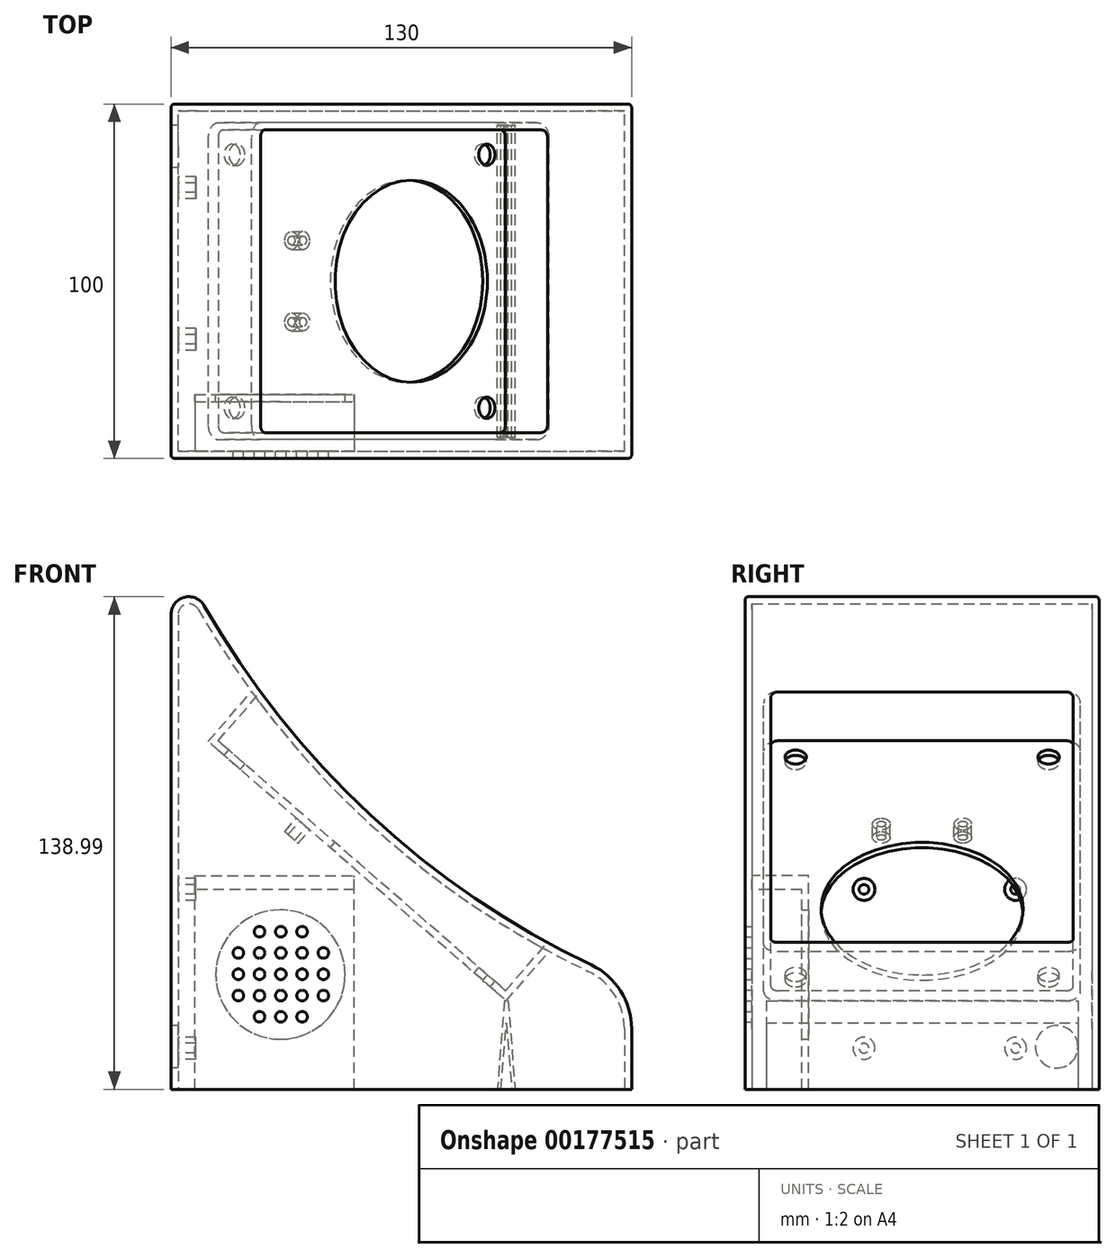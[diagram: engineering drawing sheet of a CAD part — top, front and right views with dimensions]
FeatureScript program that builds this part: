
annotation { "Feature Type Name" : "Feature", "Feature Type Description" : "" }
export const myFeature = defineFeature(function(context is Context, id is Id, definition is map)
    precondition{}
    {
        {
            var Q0;
            Q0=qCreatedBy(makeId("Front.planeOp"),FACE);
            var sketch = newSketch(context, id + "F0", { "sketchPlane" : qUnion([Q0])});
            skLineSegment(sketch, "E0", {"start": v(-84.02, -67.29) * mm, "end": v(45.98, -67.29) * mm});
            skPoint(sketch, "E1.visualSharp", {"position": v(-84.02, 87.14) * mm});
            skPoint(sketch, "E2.visualSharp", {"position": v(45.98, -37.29) * mm});
            skArc(sketch, "E3", {"start": v(-74.68, 69.19) * mm, "mid": v(-23.15, 5.98) * mm, "end": v(45.98, -37.29) * mm});
            skLineSegment(sketch, "E4", {"start": v(-84.02, 66.7) * mm, "end": v(-84.02, -67.29) * mm});
            skLineSegment(sketch, "E5", {"start": v(45.98, -37.29) * mm, "end": v(45.98, -67.29) * mm});
            skArc(sketch, "E6.filletArc", {"start": v(-74.68, 69.19) * mm, "mid": v(-80.3, 71.53) * mm, "end": v(-84.02, 66.7) * mm});
            skSolve(sketch);
        }
        {
            var Q0;
            Q0=makeQuery(id+"F0.imprint","IMPRINT",FACE,{"disambiguationData":[TD([[makeQuery(id+"F0.imprint","IMPRINT",EDGE,{"derivedFrom":sQuery(id+"F0.wireOp",EDGE,"E0")}),1.0]])]});
            extrude(context, id + "F1", {"entities" : qUnion([Q0]), "depth" : 100 * mm, "symmetric" : true});
        }
        {
            var Q0;
            Q0=makeQuery(id+"F1.opExtrude","SWEPT_EDGE",EDGE,{"disambiguationData":[OSD([sQuery(id+"F0.wireOp",EDGE,"E3"),sQuery(id+"F0.wireOp",EDGE,"E5")])]});
            cPlane(context, id + "F2", {"entities" : qUnion([Q0]), "cplaneType" : CPlaneType.LINE_ANGLE, "offset" : 25 * mm, "angle" : 41 * degree, "width" : 150 * mm, "height" : 150 * mm});
        }
        {
            var Q0;
            Q0=qCreatedBy(id+"F2.planeOp",FACE);
            var sketch = newSketch(context, id + "F3", { "sketchPlane" : qUnion([Q0])});
            skLineSegment(sketch, "E7.bottom", {"start": v(31.75, 42.7) * mm, "end": v(-71.75, 42.7) * mm});
            skLineSegment(sketch, "E7.top", {"start": v(31.75, -42.7) * mm, "end": v(-71.75, -42.7) * mm});
            skLineSegment(sketch, "E7.left", {"start": v(33.75, 40.7) * mm, "end": v(33.75, -40.7) * mm});
            skLineSegment(sketch, "E7.right", {"start": v(-73.75, 40.7) * mm, "end": v(-73.75, -40.7) * mm});
            skPoint(sketch, "E7.middle", {"position": v(-20, 0) * mm});
            skPoint(sketch, "E8.visualSharp", {"position": v(-73.75, -42.7) * mm});
            skArc(sketch, "E8.filletArc", {"start": v(-73.75, -40.7) * mm, "mid": v(-73.16, -42.11) * mm, "end": v(-71.75, -42.7) * mm});
            skPoint(sketch, "E9.visualSharp", {"position": v(-73.75, 42.7) * mm});
            skArc(sketch, "E9.filletArc", {"start": v(-71.75, 42.7) * mm, "mid": v(-73.16, 42.11) * mm, "end": v(-73.75, 40.7) * mm});
            skPoint(sketch, "E10.visualSharp", {"position": v(33.75, 42.7) * mm});
            skArc(sketch, "E10.filletArc", {"start": v(33.75, 40.7) * mm, "mid": v(33.16, 42.11) * mm, "end": v(31.75, 42.7) * mm});
            skPoint(sketch, "E11.visualSharp", {"position": v(33.75, -42.7) * mm});
            skArc(sketch, "E11.filletArc", {"start": v(31.75, -42.7) * mm, "mid": v(33.16, -42.11) * mm, "end": v(33.75, -40.7) * mm});
            skCircle(sketch, "E12", {"center": v(-1.55, 0) * mm, "radius": 28.5 * mm});
            skCircle(sketch, "E13", {"center": v(-66.75, -35.7) * mm, "radius": 3 * mm});
            skCircle(sketch, "E14", {"center": v(-66.75, 35.7) * mm, "radius": 3 * mm});
            skCircle(sketch, "E15", {"center": v(26.75, 35.7) * mm, "radius": 3 * mm});
            skCircle(sketch, "E16", {"center": v(26.75, -35.7) * mm, "radius": 3 * mm});
            skSolve(sketch);
        }
        {
            var Q0;
            Q0=makeQuery(id+"F3.imprint","IMPRINT",FACE,{"disambiguationData":[TD([[makeQuery(id+"F3.imprint","IMPRINT",EDGE,{"derivedFrom":sQuery(id+"F3.wireOp",EDGE,"E7.bottom")}),1.0]])]});
            var Q1;
            Q1=makeQuery(id+"F3.imprint","IMPRINT",FACE,{"disambiguationData":[TD([[makeQuery(id+"F3.imprint","IMPRINT",EDGE,{"derivedFrom":sQuery(id+"F3.wireOp",EDGE,"E12")}),1.0]])]});
            var Q2;
            Q2=makeQuery(id+"F3.imprint","IMPRINT",FACE,{"disambiguationData":[TD([[makeQuery(id+"F3.imprint","IMPRINT",EDGE,{"derivedFrom":sQuery(id+"F3.wireOp",EDGE,"E14")}),1.0]])]});
            var Q3;
            Q3=makeQuery(id+"F3.imprint","IMPRINT",FACE,{"disambiguationData":[TD([[makeQuery(id+"F3.imprint","IMPRINT",EDGE,{"derivedFrom":sQuery(id+"F3.wireOp",EDGE,"E15")}),1.0]])]});
            var Q4;
            Q4=makeQuery(id+"F3.imprint","IMPRINT",FACE,{"disambiguationData":[TD([[makeQuery(id+"F3.imprint","IMPRINT",EDGE,{"derivedFrom":sQuery(id+"F3.wireOp",EDGE,"E16")}),1.0]])]});
            var Q5;
            Q5=makeQuery(id+"F3.imprint","IMPRINT",FACE,{"disambiguationData":[TD([[makeQuery(id+"F3.imprint","IMPRINT",EDGE,{"derivedFrom":sQuery(id+"F3.wireOp",EDGE,"E13")}),1.0]])]});
            extrude(context, id + "F4", {"entities" : qUnion([Q0, Q1, Q2, Q3, Q4, Q5]), "operationType" : NewBodyOperationType.REMOVE, "oppositeDirection" : true, "depth" : 25 * mm});
        }
        {
            var Q0;
            Q0=makeQuery(id+"F1.opExtrude","SWEPT_EDGE",EDGE,{"disambiguationData":[OSD([sQuery(id+"F0.wireOp",EDGE,"E3"),sQuery(id+"F0.wireOp",EDGE,"E5")])]});
            fillet(context, id + "F5", {"entities" : qUnion([Q0]), "radius" : 20 * mm, "tangentPropagation" : true, "allowEdgeOverflow" : false});
        }
        {
            var Q0;
            Q0=makeQuery(id+"F1.opExtrude","SWEPT_FACE",FACE,{"disambiguationData":[OSD([sQuery(id+"F0.wireOp",EDGE,"E0")])]});
            shell(context, id + "F6", {"entities" : qUnion([Q0]), "thickness" : 2 * mm});
        }
        {
            var Q0;
            Q0=makeQuery(id+"F3.imprint","IMPRINT",FACE,{"disambiguationData":[TD([[makeQuery(id+"F3.imprint","IMPRINT",EDGE,{"derivedFrom":sQuery(id+"F3.wireOp",EDGE,"E12")}),1.0]])]});
            var Q1;
            Q1=makeQuery(id+"F3.imprint","IMPRINT",FACE,{"disambiguationData":[TD([[makeQuery(id+"F3.imprint","IMPRINT",EDGE,{"derivedFrom":sQuery(id+"F3.wireOp",EDGE,"E14")}),1.0]])]});
            var Q2;
            Q2=makeQuery(id+"F3.imprint","IMPRINT",FACE,{"disambiguationData":[TD([[makeQuery(id+"F3.imprint","IMPRINT",EDGE,{"derivedFrom":sQuery(id+"F3.wireOp",EDGE,"E13")}),1.0]])]});
            var Q3;
            Q3=makeQuery(id+"F3.imprint","IMPRINT",FACE,{"disambiguationData":[TD([[makeQuery(id+"F3.imprint","IMPRINT",EDGE,{"derivedFrom":sQuery(id+"F3.wireOp",EDGE,"E15")}),1.0]])]});
            var Q4;
            Q4=makeQuery(id+"F3.imprint","IMPRINT",FACE,{"disambiguationData":[TD([[makeQuery(id+"F3.imprint","IMPRINT",EDGE,{"derivedFrom":sQuery(id+"F3.wireOp",EDGE,"E16")}),1.0]])]});
            extrude(context, id + "F7", {"entities" : qUnion([Q0, Q1, Q2, Q3, Q4]), "operationType" : NewBodyOperationType.REMOVE, "oppositeDirection" : true, "depth" : 40 * mm});
        }
        {
            var Q0;
            Q0=makeQuery(id+"F1.opExtrude","SWEPT_FACE",FACE,{"disambiguationData":[OSD([sQuery(id+"F0.wireOp",EDGE,"E4")])]});
            var sketch = newSketch(context, id + "F8", { "sketchPlane" : qUnion([Q0])});
            skCircle(sketch, "E17", {"center": v(0, 42.55) * mm, "radius": 25 * mm, "construction": true});
            skLineSegment(sketch, "E18", {"start": v(0, 0) * mm, "end": v(0, -62.03) * mm, "construction": true});
            skLineSegment(sketch, "E19", {"start": v(-40.29, 42.55) * mm, "end": v(40.58, 42.55) * mm, "construction": true});
            skLineSegment(sketch, "E20", {"start": v(-40.29, 48.55) * mm, "end": v(40.58, 48.55) * mm, "construction": true});
            skLineSegment(sketch, "E21", {"start": v(-40.29, 36.55) * mm, "end": v(40.58, 36.55) * mm, "construction": true});
            skLineSegment(sketch, "E22", {"start": v(-40.29, 30.55) * mm, "end": v(40.58, 30.55) * mm, "construction": true});
            skLineSegment(sketch, "E23", {"start": v(-40.29, 54.55) * mm, "end": v(40.58, 54.55) * mm, "construction": true});
            skLineSegment(sketch, "E24", {"start": v(-6, 0) * mm, "end": v(-6, -62.03) * mm, "construction": true});
            skLineSegment(sketch, "E25", {"start": v(6, 0) * mm, "end": v(6, -62.03) * mm, "construction": true});
            skLineSegment(sketch, "E26", {"start": v(12, 0) * mm, "end": v(12, -62.03) * mm, "construction": true});
            skLineSegment(sketch, "E27", {"start": v(-12, 0) * mm, "end": v(-12, -62.03) * mm, "construction": true});
            skCircle(sketch, "E28", {"center": v(0, 42.55) * mm, "radius": 1.5 * mm});
            skCircle(sketch, "E29", {"center": v(6, 42.55) * mm, "radius": 1.5 * mm});
            skCircle(sketch, "E30", {"center": v(12, 42.55) * mm, "radius": 1.5 * mm});
            skCircle(sketch, "E31", {"center": v(-6, 42.55) * mm, "radius": 1.5 * mm});
            skCircle(sketch, "E32", {"center": v(-12, 42.55) * mm, "radius": 1.5 * mm});
            skCircle(sketch, "E33", {"center": v(0, 48.55) * mm, "radius": 1.5 * mm});
            skCircle(sketch, "E34", {"center": v(6, 48.55) * mm, "radius": 1.5 * mm});
            skCircle(sketch, "E35", {"center": v(-6, 48.55) * mm, "radius": 1.5 * mm});
            skCircle(sketch, "E36", {"center": v(-6, 54.55) * mm, "radius": 1.5 * mm});
            skCircle(sketch, "E37", {"center": v(0, 54.55) * mm, "radius": 1.5 * mm});
            skCircle(sketch, "E38", {"center": v(6, 54.55) * mm, "radius": 1.5 * mm});
            skCircle(sketch, "E39", {"center": v(12, 48.55) * mm, "radius": 1.5 * mm});
            skCircle(sketch, "E40", {"center": v(12, 36.55) * mm, "radius": 1.5 * mm});
            skCircle(sketch, "E41", {"center": v(6, 36.55) * mm, "radius": 1.5 * mm});
            skCircle(sketch, "E42", {"center": v(0, 36.55) * mm, "radius": 1.5 * mm});
            skCircle(sketch, "E43", {"center": v(-6, 36.55) * mm, "radius": 1.5 * mm});
            skCircle(sketch, "E44", {"center": v(-12, 36.55) * mm, "radius": 1.5 * mm});
            skCircle(sketch, "E45", {"center": v(-6, 30.55) * mm, "radius": 1.5 * mm});
            skCircle(sketch, "E46", {"center": v(0, 30.55) * mm, "radius": 1.5 * mm});
            skCircle(sketch, "E47", {"center": v(6, 30.55) * mm, "radius": 1.5 * mm});
            skCircle(sketch, "E48", {"center": v(-12, 48.55) * mm, "radius": 1.5 * mm});
            skCircle(sketch, "E49", {"center": v(-38, -55.29) * mm, "radius": 6 * mm});
            skLineSegment(sketch, "E50.bottom", {"start": v(42.5, -55.96) * mm, "end": v(-42.5, -55.96) * mm, "construction": true});
            skLineSegment(sketch, "E50.top", {"start": v(42.5, 0.04) * mm, "end": v(-42.5, 0.04) * mm, "construction": true});
            skLineSegment(sketch, "E50.left", {"start": v(42.5, -55.96) * mm, "end": v(42.5, 0.04) * mm, "construction": true});
            skLineSegment(sketch, "E50.right", {"start": v(-42.5, -55.96) * mm, "end": v(-42.5, 0.04) * mm, "construction": true});
            skPoint(sketch, "E50.middle", {"position": v(0, -27.96) * mm});
            skSolve(sketch);
        }
        {
            var Q0;
            Q0=makeQuery(id+"F8.imprint","IMPRINT",FACE,{"disambiguationData":[TD([[makeQuery(id+"F8.imprint","IMPRINT",EDGE,{"derivedFrom":sQuery(id+"F8.wireOp",EDGE,"E49")}),1.0]])]});
            extrude(context, id + "F9", {"entities" : qUnion([Q0]), "operationType" : NewBodyOperationType.REMOVE, "oppositeDirection" : true, "depth" : 25 * mm});
        }
        {
            var Q0;
            Q0=makeQuery(id+"F1.opExtrude","CAP_EDGE",EDGE,{"disambiguationData":[OSD([sQuery(id+"F0.wireOp",EDGE,"E3")])],"isStart":false});
            var Q1;
            Q1=makeQuery(id+"F1.opExtrude","CAP_EDGE",EDGE,{"disambiguationData":[OSD([sQuery(id+"F0.wireOp",EDGE,"E3")])],"isStart":true});
            fillet(context, id + "F10", {"entities" : qUnion([Q0, Q1]), "radius" : 1 * mm, "tangentPropagation" : true, "allowEdgeOverflow" : false});
        }
        {
            var Q0;
            Q0=makeQuery(id+"F6.opShell","OFFSET_FACE",FACE,{"disambiguationData":[OSD([sQuery(id+"F3.wireOp",EDGE,"E7.bottom"),sQuery(id+"F3.wireOp",EDGE,"E7.top"),sQuery(id+"F3.wireOp",EDGE,"E7.left"),sQuery(id+"F3.wireOp",EDGE,"E7.right"),sQuery(id+"F3.wireOp",EDGE,"E8.filletArc"),sQuery(id+"F3.wireOp",EDGE,"E9.filletArc"),sQuery(id+"F3.wireOp",EDGE,"E10.filletArc"),sQuery(id+"F3.wireOp",EDGE,"E11.filletArc")])]});
            cPlane(context, id + "F11", {"entities" : qUnion([Q0]), "cplaneType" : CPlaneType.OFFSET, "offset" : 0 * mm, "width" : 150 * mm, "height" : 150 * mm});
        }
        {
            var Q0;
            Q0=qCreatedBy(id+"F11.planeOp",FACE);
            var sketch = newSketch(context, id + "F12", { "sketchPlane" : qUnion([Q0])});
            skLineSegment(sketch, "E51.bottom", {"start": v(-38, 14) * mm, "end": v(-62, 14) * mm, "construction": true});
            skLineSegment(sketch, "E51.top", {"start": v(-38, -14) * mm, "end": v(-62, -14) * mm, "construction": true});
            skLineSegment(sketch, "E51.left", {"start": v(-38, 14) * mm, "end": v(-38, -14) * mm, "construction": true});
            skLineSegment(sketch, "E51.right", {"start": v(-62, 14) * mm, "end": v(-62, -14) * mm, "construction": true});
            skPoint(sketch, "E51.middle", {"position": v(-50, 0) * mm});
            skCircle(sketch, "E52", {"center": v(-40.24, 11.5) * mm, "radius": 1.25 * mm});
            skCircle(sketch, "E53", {"center": v(-40.24, -11.5) * mm, "radius": 1.25 * mm});
            skCircle(sketch, "E54", {"center": v(-40.24, 11.5) * mm, "radius": 2.5 * mm});
            skCircle(sketch, "E55", {"center": v(-40.24, -11.5) * mm, "radius": 2.5 * mm});
            skSolve(sketch);
        }
        {
            var Q0;
            {var subQ0=sQuery(id+"F0.wireOp",EDGE,"E6.filletArc");var subQ1=sQuery(id+"F0.wireOp",EDGE,"E5");var subQ2=sQuery(id+"F0.wireOp",EDGE,"E4");var subQ3=sQuery(id+"F0.wireOp",EDGE,"E3");var subQ4=sQuery(id+"F0.wireOp",EDGE,"E0");Q0=makeQuery(id+"F6.opShell","OFFSET_FACE",FACE,{"disambiguationData":[OSD([subQ4,subQ3,subQ2,subQ1,subQ0]),TDD([makeQuery(id+"F1.opExtrude","CAP_FACE",FACE,{"disambiguationData":[OSD([subQ4,subQ3,subQ2,subQ1,subQ0])],"isStart":false})])]});}
            var sketch = newSketch(context, id + "F13", { "sketchPlane" : qUnion([Q0])});
            skPoint(sketch, "E56.centerSnap0", {"position": v(36.97, -30.82) * mm});
            skCircle(sketch, "E57", {"center": v(53.03, -34.83) * mm, "radius": 1.5 * mm});
            skCircle(sketch, "E58", {"center": v(59.03, -34.83) * mm, "radius": 1.5 * mm});
            skCircle(sketch, "E59", {"center": v(65.03, -34.83) * mm, "radius": 1.5 * mm});
            skCircle(sketch, "E60", {"center": v(47.03, -34.83) * mm, "radius": 1.5 * mm});
            skCircle(sketch, "E61", {"center": v(41.03, -34.83) * mm, "radius": 1.5 * mm});
            skCircle(sketch, "E62", {"center": v(53.03, -28.83) * mm, "radius": 1.5 * mm});
            skCircle(sketch, "E63", {"center": v(59.03, -28.83) * mm, "radius": 1.5 * mm});
            skCircle(sketch, "E64", {"center": v(47.03, -28.83) * mm, "radius": 1.5 * mm});
            skCircle(sketch, "E65", {"center": v(47.03, -22.83) * mm, "radius": 1.5 * mm});
            skCircle(sketch, "E66", {"center": v(53.03, -22.83) * mm, "radius": 1.5 * mm});
            skCircle(sketch, "E67", {"center": v(59.03, -22.83) * mm, "radius": 1.5 * mm});
            skCircle(sketch, "E68", {"center": v(65.03, -28.83) * mm, "radius": 1.5 * mm});
            skCircle(sketch, "E69", {"center": v(65.03, -40.83) * mm, "radius": 1.5 * mm});
            skCircle(sketch, "E70", {"center": v(59.03, -40.83) * mm, "radius": 1.5 * mm});
            skCircle(sketch, "E71", {"center": v(53.03, -40.83) * mm, "radius": 1.5 * mm});
            skCircle(sketch, "E72", {"center": v(47.03, -40.83) * mm, "radius": 1.5 * mm});
            skCircle(sketch, "E73", {"center": v(41.03, -40.83) * mm, "radius": 1.5 * mm});
            skCircle(sketch, "E74", {"center": v(47.03, -46.83) * mm, "radius": 1.5 * mm});
            skCircle(sketch, "E75", {"center": v(53.03, -46.83) * mm, "radius": 1.5 * mm});
            skCircle(sketch, "E76", {"center": v(59.03, -46.83) * mm, "radius": 1.5 * mm});
            skCircle(sketch, "E77", {"center": v(41.03, -28.83) * mm, "radius": 1.5 * mm});
            skLineSegment(sketch, "E78", {"start": v(65.03, -40.83) * mm, "end": v(41.03, -40.83) * mm});
            skLineSegment(sketch, "E79", {"start": v(59.03, -46.83) * mm, "end": v(47.03, -46.83) * mm});
            skLineSegment(sketch, "E80", {"start": v(65.03, -28.83) * mm, "end": v(41.03, -28.83) * mm});
            skLineSegment(sketch, "E81", {"start": v(59.03, -22.83) * mm, "end": v(47.03, -22.83) * mm});
            skSolve(sketch);
        }
        {
            var Q0;
            {var subQ0=sQuery(id+"F13.wireOp",EDGE,"E80");var subQ1=sQuery(id+"F13.wireOp",EDGE,"E64");var subQ2=makeQuery(id+"F13.imprint","INTERSECT",VERTEX,{"disambiguationData":[OD(0.0)],"derivedFrom":[subQ1,subQ0]});Q0=makeQuery(id+"F13.imprint","IMPRINT",FACE,{"disambiguationData":[TD([[makeQuery(id+"F13.imprint","IMPRINT",EDGE,{"disambiguationData":[TD([[subQ2,-1.0]])],"derivedFrom":subQ1}),1.0]])]});}
            var Q1;
            {var subQ0=sQuery(id+"F13.wireOp",EDGE,"E78");var subQ1=sQuery(id+"F13.wireOp",EDGE,"E71");var subQ2=makeQuery(id+"F13.imprint","INTERSECT",VERTEX,{"disambiguationData":[OD(0.0)],"derivedFrom":[subQ1,subQ0]});Q1=makeQuery(id+"F13.imprint","IMPRINT",FACE,{"disambiguationData":[TD([[makeQuery(id+"F13.imprint","IMPRINT",EDGE,{"disambiguationData":[TD([[subQ2,1.0]])],"derivedFrom":subQ1}),1.0]])]});}
            var Q2;
            Q2=makeQuery(id+"F13.imprint","IMPRINT",FACE,{"disambiguationData":[TD([[makeQuery(id+"F13.imprint","IMPRINT",EDGE,{"derivedFrom":sQuery(id+"F13.wireOp",EDGE,"E59")}),1.0]])]});
            var Q3;
            Q3=makeQuery(id+"F13.imprint","IMPRINT",FACE,{"disambiguationData":[TD([[makeQuery(id+"F13.imprint","IMPRINT",EDGE,{"derivedFrom":sQuery(id+"F13.wireOp",EDGE,"E60")}),1.0]])]});
            var Q4;
            {var subQ0=sQuery(id+"F13.wireOp",EDGE,"E79");var subQ1=sQuery(id+"F13.wireOp",EDGE,"E75");var subQ2=makeQuery(id+"F13.imprint","INTERSECT",VERTEX,{"disambiguationData":[OD(0.0)],"derivedFrom":[subQ1,subQ0]});Q4=makeQuery(id+"F13.imprint","IMPRINT",FACE,{"disambiguationData":[TD([[makeQuery(id+"F13.imprint","IMPRINT",EDGE,{"disambiguationData":[TD([[subQ2,-1.0]])],"derivedFrom":subQ1}),1.0]])]});}
            var Q5;
            Q5=makeQuery(id+"F13.imprint","IMPRINT",FACE,{"disambiguationData":[TD([[makeQuery(id+"F13.imprint","IMPRINT",EDGE,{"derivedFrom":sQuery(id+"F13.wireOp",EDGE,"E58")}),1.0]])]});
            var Q6;
            Q6=makeQuery(id+"F13.imprint","IMPRINT",FACE,{"disambiguationData":[TD([[makeQuery(id+"F13.imprint","IMPRINT",EDGE,{"derivedFrom":sQuery(id+"F13.wireOp",EDGE,"E74")}),1.0]])]});
            var Q7;
            {var subQ0=sQuery(id+"F13.wireOp",EDGE,"E78");var subQ1=sQuery(id+"F13.wireOp",EDGE,"E71");var subQ2=makeQuery(id+"F13.imprint","INTERSECT",VERTEX,{"disambiguationData":[OD(0.0)],"derivedFrom":[subQ1,subQ0]});Q7=makeQuery(id+"F13.imprint","IMPRINT",FACE,{"disambiguationData":[TD([[makeQuery(id+"F13.imprint","IMPRINT",EDGE,{"disambiguationData":[TD([[subQ2,-1.0]])],"derivedFrom":subQ1}),1.0]])]});}
            var Q8;
            {var subQ0=sQuery(id+"F13.wireOp",EDGE,"E79");var subQ1=sQuery(id+"F13.wireOp",EDGE,"E75");var subQ2=makeQuery(id+"F13.imprint","INTERSECT",VERTEX,{"disambiguationData":[OD(0.0)],"derivedFrom":[subQ1,subQ0]});Q8=makeQuery(id+"F13.imprint","IMPRINT",FACE,{"disambiguationData":[TD([[makeQuery(id+"F13.imprint","IMPRINT",EDGE,{"disambiguationData":[TD([[subQ2,1.0]])],"derivedFrom":subQ1}),1.0]])]});}
            var Q9;
            {var subQ0=sQuery(id+"F13.wireOp",EDGE,"E80");var subQ1=sQuery(id+"F13.wireOp",EDGE,"E63");var subQ2=makeQuery(id+"F13.imprint","INTERSECT",VERTEX,{"disambiguationData":[OD(0.0)],"derivedFrom":[subQ1,subQ0]});Q9=makeQuery(id+"F13.imprint","IMPRINT",FACE,{"disambiguationData":[TD([[makeQuery(id+"F13.imprint","IMPRINT",EDGE,{"disambiguationData":[TD([[subQ2,-1.0]])],"derivedFrom":subQ1}),1.0]])]});}
            var Q10;
            {var subQ0=sQuery(id+"F13.wireOp",EDGE,"E81");var subQ1=sQuery(id+"F13.wireOp",EDGE,"E66");var subQ2=makeQuery(id+"F13.imprint","INTERSECT",VERTEX,{"disambiguationData":[OD(0.0)],"derivedFrom":[subQ1,subQ0]});Q10=makeQuery(id+"F13.imprint","IMPRINT",FACE,{"disambiguationData":[TD([[makeQuery(id+"F13.imprint","IMPRINT",EDGE,{"disambiguationData":[TD([[subQ2,1.0]])],"derivedFrom":subQ1}),1.0]])]});}
            var Q11;
            {var subQ0=sQuery(id+"F13.wireOp",EDGE,"E80");var subQ1=sQuery(id+"F13.wireOp",EDGE,"E64");var subQ2=makeQuery(id+"F13.imprint","INTERSECT",VERTEX,{"disambiguationData":[OD(0.0)],"derivedFrom":[subQ1,subQ0]});Q11=makeQuery(id+"F13.imprint","IMPRINT",FACE,{"disambiguationData":[TD([[makeQuery(id+"F13.imprint","IMPRINT",EDGE,{"disambiguationData":[TD([[subQ2,1.0]])],"derivedFrom":subQ1}),1.0]])]});}
            var Q12;
            Q12=makeQuery(id+"F13.imprint","IMPRINT",FACE,{"disambiguationData":[TD([[makeQuery(id+"F13.imprint","IMPRINT",EDGE,{"derivedFrom":sQuery(id+"F13.wireOp",EDGE,"E77")}),1.0]])]});
            var Q13;
            {var subQ0=sQuery(id+"F13.wireOp",EDGE,"E78");var subQ1=sQuery(id+"F13.wireOp",EDGE,"E72");var subQ2=makeQuery(id+"F13.imprint","INTERSECT",VERTEX,{"disambiguationData":[OD(0.0)],"derivedFrom":[subQ1,subQ0]});Q13=makeQuery(id+"F13.imprint","IMPRINT",FACE,{"disambiguationData":[TD([[makeQuery(id+"F13.imprint","IMPRINT",EDGE,{"disambiguationData":[TD([[subQ2,-1.0]])],"derivedFrom":subQ1}),1.0]])]});}
            var Q14;
            {var subQ0=sQuery(id+"F13.wireOp",EDGE,"E78");var subQ1=sQuery(id+"F13.wireOp",EDGE,"E70");var subQ2=makeQuery(id+"F13.imprint","INTERSECT",VERTEX,{"disambiguationData":[OD(0.0)],"derivedFrom":[subQ1,subQ0]});Q14=makeQuery(id+"F13.imprint","IMPRINT",FACE,{"disambiguationData":[TD([[makeQuery(id+"F13.imprint","IMPRINT",EDGE,{"disambiguationData":[TD([[subQ2,1.0]])],"derivedFrom":subQ1}),1.0]])]});}
            var Q15;
            {var subQ0=sQuery(id+"F13.wireOp",EDGE,"E80");var subQ1=sQuery(id+"F13.wireOp",EDGE,"E62");var subQ2=makeQuery(id+"F13.imprint","INTERSECT",VERTEX,{"disambiguationData":[OD(0.0)],"derivedFrom":[subQ1,subQ0]});Q15=makeQuery(id+"F13.imprint","IMPRINT",FACE,{"disambiguationData":[TD([[makeQuery(id+"F13.imprint","IMPRINT",EDGE,{"disambiguationData":[TD([[subQ2,1.0]])],"derivedFrom":subQ1}),1.0]])]});}
            var Q16;
            Q16=makeQuery(id+"F13.imprint","IMPRINT",FACE,{"disambiguationData":[TD([[makeQuery(id+"F13.imprint","IMPRINT",EDGE,{"derivedFrom":sQuery(id+"F13.wireOp",EDGE,"E67")}),1.0]])]});
            var Q17;
            {var subQ0=sQuery(id+"F13.wireOp",EDGE,"E80");var subQ1=sQuery(id+"F13.wireOp",EDGE,"E63");var subQ2=makeQuery(id+"F13.imprint","INTERSECT",VERTEX,{"disambiguationData":[OD(0.0)],"derivedFrom":[subQ1,subQ0]});Q17=makeQuery(id+"F13.imprint","IMPRINT",FACE,{"disambiguationData":[TD([[makeQuery(id+"F13.imprint","IMPRINT",EDGE,{"disambiguationData":[TD([[subQ2,1.0]])],"derivedFrom":subQ1}),1.0]])]});}
            var Q18;
            Q18=makeQuery(id+"F13.imprint","IMPRINT",FACE,{"disambiguationData":[TD([[makeQuery(id+"F13.imprint","IMPRINT",EDGE,{"derivedFrom":sQuery(id+"F13.wireOp",EDGE,"E65")}),1.0]])]});
            var Q19;
            {var subQ0=sQuery(id+"F13.wireOp",EDGE,"E78");var subQ1=sQuery(id+"F13.wireOp",EDGE,"E70");var subQ2=makeQuery(id+"F13.imprint","INTERSECT",VERTEX,{"disambiguationData":[OD(0.0)],"derivedFrom":[subQ1,subQ0]});Q19=makeQuery(id+"F13.imprint","IMPRINT",FACE,{"disambiguationData":[TD([[makeQuery(id+"F13.imprint","IMPRINT",EDGE,{"disambiguationData":[TD([[subQ2,-1.0]])],"derivedFrom":subQ1}),1.0]])]});}
            var Q20;
            Q20=makeQuery(id+"F13.imprint","IMPRINT",FACE,{"disambiguationData":[TD([[makeQuery(id+"F13.imprint","IMPRINT",EDGE,{"derivedFrom":sQuery(id+"F13.wireOp",EDGE,"E76")}),1.0]])]});
            var Q21;
            Q21=makeQuery(id+"F13.imprint","IMPRINT",FACE,{"disambiguationData":[TD([[makeQuery(id+"F13.imprint","IMPRINT",EDGE,{"derivedFrom":sQuery(id+"F13.wireOp",EDGE,"E57")}),1.0]])]});
            var Q22;
            Q22=makeQuery(id+"F13.imprint","IMPRINT",FACE,{"disambiguationData":[TD([[makeQuery(id+"F13.imprint","IMPRINT",EDGE,{"derivedFrom":sQuery(id+"F13.wireOp",EDGE,"E73")}),1.0]])]});
            var Q23;
            Q23=makeQuery(id+"F13.imprint","IMPRINT",FACE,{"disambiguationData":[TD([[makeQuery(id+"F13.imprint","IMPRINT",EDGE,{"derivedFrom":sQuery(id+"F13.wireOp",EDGE,"E61")}),1.0]])]});
            var Q24;
            {var subQ0=sQuery(id+"F13.wireOp",EDGE,"E78");var subQ1=sQuery(id+"F13.wireOp",EDGE,"E72");var subQ2=makeQuery(id+"F13.imprint","INTERSECT",VERTEX,{"disambiguationData":[OD(0.0)],"derivedFrom":[subQ1,subQ0]});Q24=makeQuery(id+"F13.imprint","IMPRINT",FACE,{"disambiguationData":[TD([[makeQuery(id+"F13.imprint","IMPRINT",EDGE,{"disambiguationData":[TD([[subQ2,1.0]])],"derivedFrom":subQ1}),1.0]])]});}
            var Q25;
            {var subQ0=sQuery(id+"F13.wireOp",EDGE,"E80");var subQ1=sQuery(id+"F13.wireOp",EDGE,"E62");var subQ2=makeQuery(id+"F13.imprint","INTERSECT",VERTEX,{"disambiguationData":[OD(0.0)],"derivedFrom":[subQ1,subQ0]});Q25=makeQuery(id+"F13.imprint","IMPRINT",FACE,{"disambiguationData":[TD([[makeQuery(id+"F13.imprint","IMPRINT",EDGE,{"disambiguationData":[TD([[subQ2,-1.0]])],"derivedFrom":subQ1}),1.0]])]});}
            var Q26;
            {var subQ0=sQuery(id+"F13.wireOp",EDGE,"E81");var subQ1=sQuery(id+"F13.wireOp",EDGE,"E66");var subQ2=makeQuery(id+"F13.imprint","INTERSECT",VERTEX,{"disambiguationData":[OD(0.0)],"derivedFrom":[subQ1,subQ0]});Q26=makeQuery(id+"F13.imprint","IMPRINT",FACE,{"disambiguationData":[TD([[makeQuery(id+"F13.imprint","IMPRINT",EDGE,{"disambiguationData":[TD([[subQ2,-1.0]])],"derivedFrom":subQ1}),1.0]])]});}
            var Q27;
            Q27=makeQuery(id+"F13.imprint","IMPRINT",FACE,{"disambiguationData":[TD([[makeQuery(id+"F13.imprint","IMPRINT",EDGE,{"derivedFrom":sQuery(id+"F13.wireOp",EDGE,"E69")}),1.0]])]});
            var Q28;
            Q28=makeQuery(id+"F13.imprint","IMPRINT",FACE,{"disambiguationData":[TD([[makeQuery(id+"F13.imprint","IMPRINT",EDGE,{"derivedFrom":sQuery(id+"F13.wireOp",EDGE,"E68")}),1.0]])]});
            var Q29;
            Q29=sQuery(id+"F13.wireOp",EDGE,"E81");
            var Q30;
            Q30=sQuery(id+"F13.wireOp",EDGE,"E67");
            var Q31;
            Q31=sQuery(id+"F13.wireOp",EDGE,"E65");
            var Q32;
            Q32=sQuery(id+"F13.wireOp",EDGE,"E63");
            var Q33;
            Q33=sQuery(id+"F13.wireOp",EDGE,"E58");
            var Q34;
            Q34=sQuery(id+"F13.wireOp",EDGE,"E80");
            var Q35;
            Q35=sQuery(id+"F13.wireOp",EDGE,"E78");
            var Q36;
            Q36=sQuery(id+"F13.wireOp",EDGE,"E79");
            var Q37;
            Q37=sQuery(id+"F13.wireOp",EDGE,"E70");
            var Q38;
            Q38=sQuery(id+"F13.wireOp",EDGE,"E73");
            var Q39;
            Q39=sQuery(id+"F13.wireOp",EDGE,"E72");
            var Q40;
            Q40=sQuery(id+"F13.wireOp",EDGE,"E64");
            var Q41;
            Q41=sQuery(id+"F13.wireOp",EDGE,"E76");
            var Q42;
            Q42=sQuery(id+"F13.wireOp",EDGE,"E59");
            var Q43;
            Q43=sQuery(id+"F13.wireOp",EDGE,"E57");
            var Q44;
            Q44=sQuery(id+"F13.wireOp",EDGE,"E71");
            var Q45;
            Q45=sQuery(id+"F13.wireOp",EDGE,"E77");
            var Q46;
            Q46=sQuery(id+"F13.wireOp",EDGE,"E74");
            var Q47;
            Q47=sQuery(id+"F13.wireOp",EDGE,"E68");
            var Q48;
            Q48=sQuery(id+"F13.wireOp",EDGE,"E69");
            var Q49;
            Q49=sQuery(id+"F13.wireOp",EDGE,"E75");
            var Q50;
            Q50=sQuery(id+"F13.wireOp",EDGE,"E66");
            var Q51;
            Q51=sQuery(id+"F13.wireOp",EDGE,"E61");
            var Q52;
            Q52=sQuery(id+"F13.wireOp",EDGE,"E60");
            var Q53;
            Q53=sQuery(id+"F13.wireOp",EDGE,"E62");
            extrude(context, id + "F14", {"entities" : qUnion([Q0, Q1, Q2, Q3, Q4, Q5, Q6, Q7, Q8, Q9, Q10, Q11, Q12, Q13, Q14, Q15, Q16, Q17, Q18, Q19, Q20, Q21, Q22, Q23, Q24, Q25, Q26, Q27, Q28]), "operationType" : NewBodyOperationType.REMOVE, "surfaceEntities" : qUnion([Q29, Q30, Q31, Q32, Q33, Q34, Q35, Q36, Q37, Q38, Q39, Q40, Q41, Q42, Q43, Q44, Q45, Q46, Q47, Q48, Q49, Q50, Q51, Q52, Q53]), "oppositeDirection" : true, "depth" : 25 * mm});
        }
        {
            var Q0;
            {var subQ0=sQuery(id+"F0.wireOp",EDGE,"E6.filletArc");var subQ1=sQuery(id+"F0.wireOp",EDGE,"E5");var subQ2=sQuery(id+"F0.wireOp",EDGE,"E4");var subQ3=sQuery(id+"F0.wireOp",EDGE,"E3");var subQ4=sQuery(id+"F0.wireOp",EDGE,"E0");Q0=makeQuery(id+"F6.opShell","OFFSET_FACE",FACE,{"disambiguationData":[OSD([subQ4,subQ3,subQ2,subQ1,subQ0]),TDD([makeQuery(id+"F1.opExtrude","CAP_FACE",FACE,{"disambiguationData":[OSD([subQ4,subQ3,subQ2,subQ1,subQ0])],"isStart":false})])]});}
            var sketch = newSketch(context, id + "F15", { "sketchPlane" : qUnion([Q0])});
            skLineSegment(sketch, "E82.top", {"start": v(77.3, -7) * mm, "end": v(32.3, -7) * mm});
            skLineSegment(sketch, "E82.left", {"start": v(77.3, -11) * mm, "end": v(77.3, -7) * mm});
            skLineSegment(sketch, "E82.right", {"start": v(32.3, -11) * mm, "end": v(32.3, -7) * mm});
            skPoint(sketch, "E82.middle", {"position": v(54.8, -9) * mm});
            skLineSegment(sketch, "E83", {"start": v(77.3, -11) * mm, "end": v(77.3, -56) * mm, "construction": true});
            skLineSegment(sketch, "E84", {"start": v(77.3, -33.5) * mm, "end": v(33.54, -33.5) * mm, "construction": true});
            skLineSegment(sketch, "E85", {"start": v(32.3, -11) * mm, "end": v(77.3, -11) * mm});
            skSolve(sketch);
        }
        {
            var Q0;
            Q0 = qSketchRegion(id + "F15", true);
            extrude(context, id + "F16", {"entities" : qUnion([Q0]), "operationType" : NewBodyOperationType.ADD, "depth" : 16 * mm});
        }
        {
            var Q0;
            Q0=makeQuery(id+"F16.opExtrude","SWEPT_FACE",FACE,{"disambiguationData":[OSD([sQuery(id+"F15.wireOp",EDGE,"E85")])]});
            var sketch = newSketch(context, id + "F17", { "sketchPlane" : qUnion([Q0])});
            skLineSegment(sketch, "E86.bottom", {"start": v(-77.3, 32) * mm, "end": v(-32.3, 32) * mm});
            skLineSegment(sketch, "E86.top", {"start": v(-77.3, 34) * mm, "end": v(-32.3, 34) * mm});
            skLineSegment(sketch, "E86.left", {"start": v(-77.3, 32) * mm, "end": v(-77.3, 34) * mm});
            skLineSegment(sketch, "E86.right", {"start": v(-32.3, 32) * mm, "end": v(-32.3, 34) * mm});
            skSolve(sketch);
        }
        {
            var Q0;
            Q0=makeQuery(id+"F17.imprint","IMPRINT",FACE,{"disambiguationData":[TD([[makeQuery(id+"F17.imprint","IMPRINT",EDGE,{"derivedFrom":sQuery(id+"F17.wireOp",EDGE,"E86.bottom")}),-1.0]])]});
            var Q1;
            Q1=makeQuery(id+"F1.opExtrude","SWEPT_FACE",FACE,{"disambiguationData":[OSD([sQuery(id+"F0.wireOp",EDGE,"E0")])]});
            extrude(context, id + "F18", {"entities" : qUnion([Q0]), "operationType" : NewBodyOperationType.ADD, "endBound" : BoundingType.UP_TO_SURFACE, "endBoundEntityFace" : qUnion([Q1]), "depth" : 50 * mm});
        }
        {
            var Q0;
            Q0=makeQuery(id+"F18.boolean.opBoolean","MERGE",FACE,{"derivedFrom":[makeQuery(id+"F16.opExtrude","CAP_FACE",FACE,{"disambiguationData":[OSD([sQuery(id+"F15.wireOp",EDGE,"E82.bottom"),sQuery(id+"F15.wireOp",EDGE,"E82.top"),sQuery(id+"F15.wireOp",EDGE,"E82.left"),sQuery(id+"F15.wireOp",EDGE,"E82.right")])],"isStart":false}),makeQuery(id+"F18.opExtrude","SWEPT_FACE",FACE,{"disambiguationData":[OSD([sQuery(id+"F17.wireOp",EDGE,"CFtCSqfR-IfQe-7JBa-NznS-rNRl7jurEekL.bottom")])]})]});
            var sketch = newSketch(context, id + "F19", { "sketchPlane" : qUnion([Q0])});
            skCircle(sketch, "E87", {"center": v(53.14, -34.91) * mm, "radius": 18.25 * mm});
            skSolve(sketch);
        }
        {
            var Q0;
            Q0=makeQuery(id+"F19.imprint","IMPRINT",FACE,{"disambiguationData":[TD([[makeQuery(id+"F19.imprint","IMPRINT",EDGE,{"derivedFrom":sQuery(id+"F19.wireOp",EDGE,"E87")}),1.0]])]});
            var Q1;
            Q1=sQuery(id+"F19.wireOp",EDGE,"E87");
            extrude(context, id + "F20", {"entities" : qUnion([Q0]), "operationType" : NewBodyOperationType.REMOVE, "surfaceEntities" : qUnion([Q1]), "oppositeDirection" : true, "depth" : 5 * mm});
        }
        {
            var Q0;
            Q0=makeQuery(id+"F6.opShell","OFFSET_FACE",FACE,{"disambiguationData":[OSD([sQuery(id+"F0.wireOp",EDGE,"E4")])]});
            var sketch = newSketch(context, id + "F21", { "sketchPlane" : qUnion([Q0])});
            skLineSegment(sketch, "E88.bottom", {"start": v(-23, -62.29) * mm, "end": v(33, -62.29) * mm, "construction": true});
            skLineSegment(sketch, "E88.top", {"start": v(-23, 22.71) * mm, "end": v(33, 22.71) * mm, "construction": true});
            skLineSegment(sketch, "E88.left", {"start": v(-23, -62.29) * mm, "end": v(-23, 22.71) * mm, "construction": true});
            skLineSegment(sketch, "E88.right", {"start": v(33, -62.29) * mm, "end": v(33, 22.71) * mm, "construction": true});
            skCircle(sketch, "E89", {"center": v(26.4, -55.69) * mm, "radius": 3.1 * mm});
            skCircle(sketch, "E90", {"center": v(26.4, -55.69) * mm, "radius": 1.38 * mm});
            skCircle(sketch, "E91", {"center": v(-16.4, -55.69) * mm, "radius": 3.1 * mm});
            skCircle(sketch, "E92", {"center": v(-16.4, -55.69) * mm, "radius": 1.38 * mm});
            skCircle(sketch, "E93", {"center": v(-16.4, -10.89) * mm, "radius": 3.1 * mm});
            skCircle(sketch, "E94", {"center": v(-16.4, -10.89) * mm, "radius": 1.37 * mm});
            skCircle(sketch, "E95", {"center": v(26.4, -10.89) * mm, "radius": 3.1 * mm});
            skCircle(sketch, "E96", {"center": v(26.4, -10.89) * mm, "radius": 1.38 * mm});
            skLineSegment(sketch, "E97", {"start": v(43.64, -4.29) * mm, "end": v(-31, -4.29) * mm, "construction": true});
            skSolve(sketch);
        }
        {
            var Q0;
            Q0=makeQuery(id+"F21.imprint","IMPRINT",FACE,{"disambiguationData":[TD([[makeQuery(id+"F21.imprint","IMPRINT",EDGE,{"derivedFrom":sQuery(id+"F21.wireOp",EDGE,"E91")}),1.0]])]});
            var Q1;
            Q1=makeQuery(id+"F21.imprint","IMPRINT",FACE,{"disambiguationData":[TD([[makeQuery(id+"F21.imprint","IMPRINT",EDGE,{"derivedFrom":sQuery(id+"F21.wireOp",EDGE,"E93")}),1.0]])]});
            var Q2;
            Q2=makeQuery(id+"F21.imprint","IMPRINT",FACE,{"disambiguationData":[TD([[makeQuery(id+"F21.imprint","IMPRINT",EDGE,{"derivedFrom":sQuery(id+"F21.wireOp",EDGE,"E95")}),1.0]])]});
            var Q3;
            Q3=makeQuery(id+"F21.imprint","IMPRINT",FACE,{"disambiguationData":[TD([[makeQuery(id+"F21.imprint","IMPRINT",EDGE,{"derivedFrom":sQuery(id+"F21.wireOp",EDGE,"E89")}),1.0]])]});
            extrude(context, id + "F22", {"entities" : qUnion([Q0, Q1, Q2, Q3]), "operationType" : NewBodyOperationType.ADD, "depth" : 5 * mm});
        }
        {
            var Q0;
            Q0=makeQuery(id+"F1.opExtrude","CAP_FACE",FACE,{"disambiguationData":[OSD([sQuery(id+"F0.wireOp",EDGE,"E0"),sQuery(id+"F0.wireOp",EDGE,"E3"),sQuery(id+"F0.wireOp",EDGE,"E4"),sQuery(id+"F0.wireOp",EDGE,"E5"),sQuery(id+"F0.wireOp",EDGE,"E6.filletArc")])],"isStart":true});
            cPlane(context, id + "F23", {"entities" : qUnion([Q0]), "cplaneType" : CPlaneType.OFFSET, "offset" : 6 * mm, "oppositeDirection" : true, "width" : 150 * mm, "height" : 150 * mm});
        }
        {
            var Q0;
            Q0=qCreatedBy(id+"F23.planeOp",FACE);
            var sketch = newSketch(context, id + "F24", { "sketchPlane" : qUnion([Q0])});
            skLineSegment(sketch, "E98", {"start": v(-11.1, -42.3) * mm, "end": v(-10.1, -42.3) * mm});
            skLineSegment(sketch, "E99", {"start": v(-11.1, -42.3) * mm, "end": v(-13.1, -67.29) * mm});
            skLineSegment(sketch, "E100", {"start": v(-10.1, -42.3) * mm, "end": v(-8.1, -67.29) * mm});
            skLineSegment(sketch, "E101", {"start": v(-13.1, -67.29) * mm, "end": v(-12.1, -67.29) * mm});
            skLineSegment(sketch, "E102", {"start": v(-8.1, -67.29) * mm, "end": v(-9.1, -67.29) * mm});
            skLineSegment(sketch, "E103", {"start": v(-9.1, -67.29) * mm, "end": v(-10.6, -48.55) * mm});
            skLineSegment(sketch, "E104", {"start": v(-10.6, -48.55) * mm, "end": v(-12.1, -67.29) * mm});
            skSolve(sketch);
        }
        {
            var Q0;
            Q0=makeQuery(id+"F24.imprint","IMPRINT",FACE,{"disambiguationData":[TD([[makeQuery(id+"F24.imprint","IMPRINT",EDGE,{"derivedFrom":sQuery(id+"F24.wireOp",EDGE,"E98")}),-1.0]])]});
            extrude(context, id + "F25", {"entities" : qUnion([Q0]), "oppositeDirection" : true, "depth" : 88 * mm});
        }
        {
            var Q0;
            Q0=makeQuery(id+"F12.imprint","IMPRINT",FACE,{"disambiguationData":[TD([[makeQuery(id+"F12.imprint","IMPRINT",EDGE,{"derivedFrom":sQuery(id+"F12.wireOp",EDGE,"E52")}),-1.0]])]});
            var Q1;
            Q1=makeQuery(id+"F12.imprint","IMPRINT",FACE,{"disambiguationData":[TD([[makeQuery(id+"F12.imprint","IMPRINT",EDGE,{"derivedFrom":sQuery(id+"F12.wireOp",EDGE,"E53")}),-1.0]])]});
            extrude(context, id + "F26", {"entities" : qUnion([Q0, Q1]), "operationType" : NewBodyOperationType.ADD, "depth" : 5 * mm});
        }
        {
            var Q0;
            Q0=makeQuery(id+"F21.imprint","IMPRINT",FACE,{"disambiguationData":[TD([[makeQuery(id+"F21.imprint","IMPRINT",EDGE,{"derivedFrom":sQuery(id+"F21.wireOp",EDGE,"E89")}),-1.0]])]});
            cPlane(context, id + "F27", {"entities" : qUnion([Q0]), "cplaneType" : CPlaneType.OFFSET, "offset" : 5 * mm, "width" : 150 * mm, "height" : 150 * mm});
        }
    });
